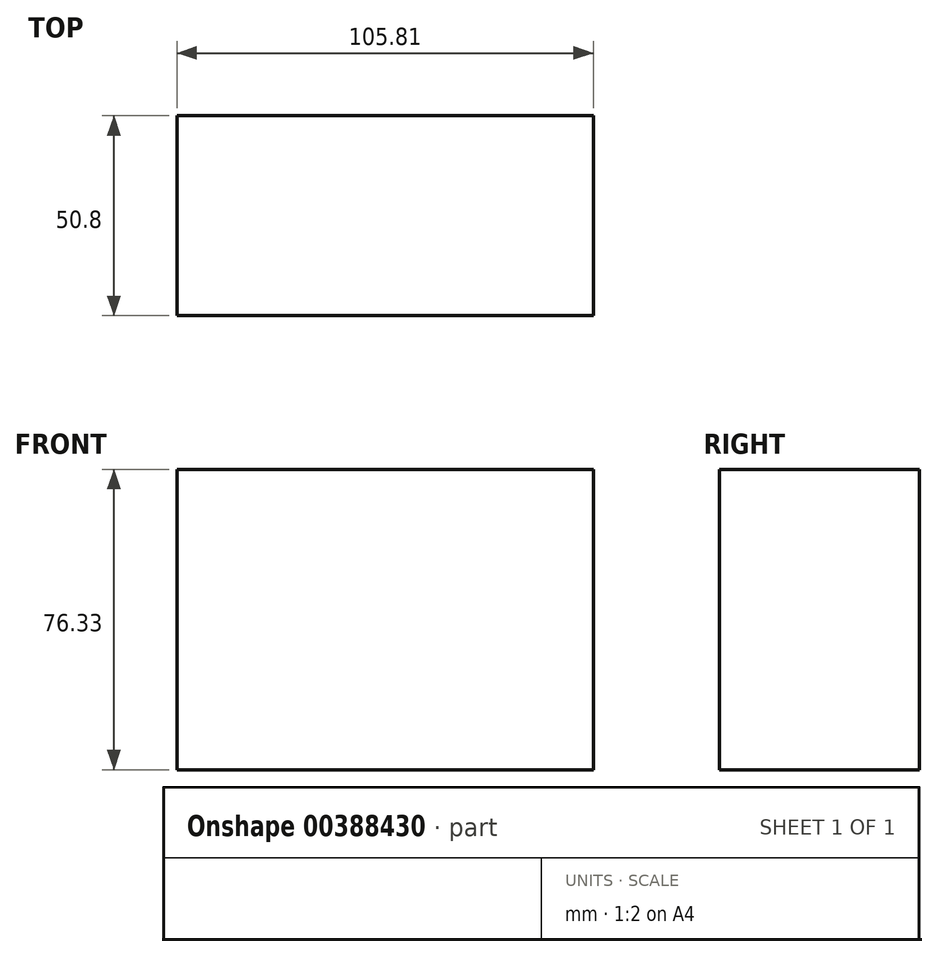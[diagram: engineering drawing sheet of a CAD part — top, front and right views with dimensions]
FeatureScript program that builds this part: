
annotation { "Feature Type Name" : "Feature", "Feature Type Description" : "" }
export const myFeature = defineFeature(function(context is Context, id is Id, definition is map)
    precondition{}
    {
        {
            var Q0;
            Q0=qCreatedBy(makeId("Front.planeOp"),FACE);
            var sketch = newSketch(context, id + "F0", { "sketchPlane" : qUnion([Q0])});
            skLineSegment(sketch, "E0.bottom", {"start": v(-48.93, 39.05) * mm, "end": v(56.88, 39.05) * mm});
            skLineSegment(sketch, "E0.top", {"start": v(-48.93, -37.28) * mm, "end": v(56.88, -37.28) * mm});
            skLineSegment(sketch, "E0.left", {"start": v(-48.93, 39.05) * mm, "end": v(-48.93, -37.28) * mm});
            skLineSegment(sketch, "E0.right", {"start": v(56.88, 39.05) * mm, "end": v(56.88, -37.28) * mm});
            skSolve(sketch);
        }
        {
            var Q0;
            Q0=makeQuery(id+"F0.imprint","IMPRINT",FACE,{"disambiguationData":[TD([[makeQuery(id+"F0.imprint","IMPRINT",EDGE,{"derivedFrom":sQuery(id+"F0.wireOp",EDGE,"E0.bottom")}),-1.0]])]});
            extrude(context, id + "F1", {"entities" : qUnion([Q0]), "depth" : 50.8 * mm});
        }
    });
